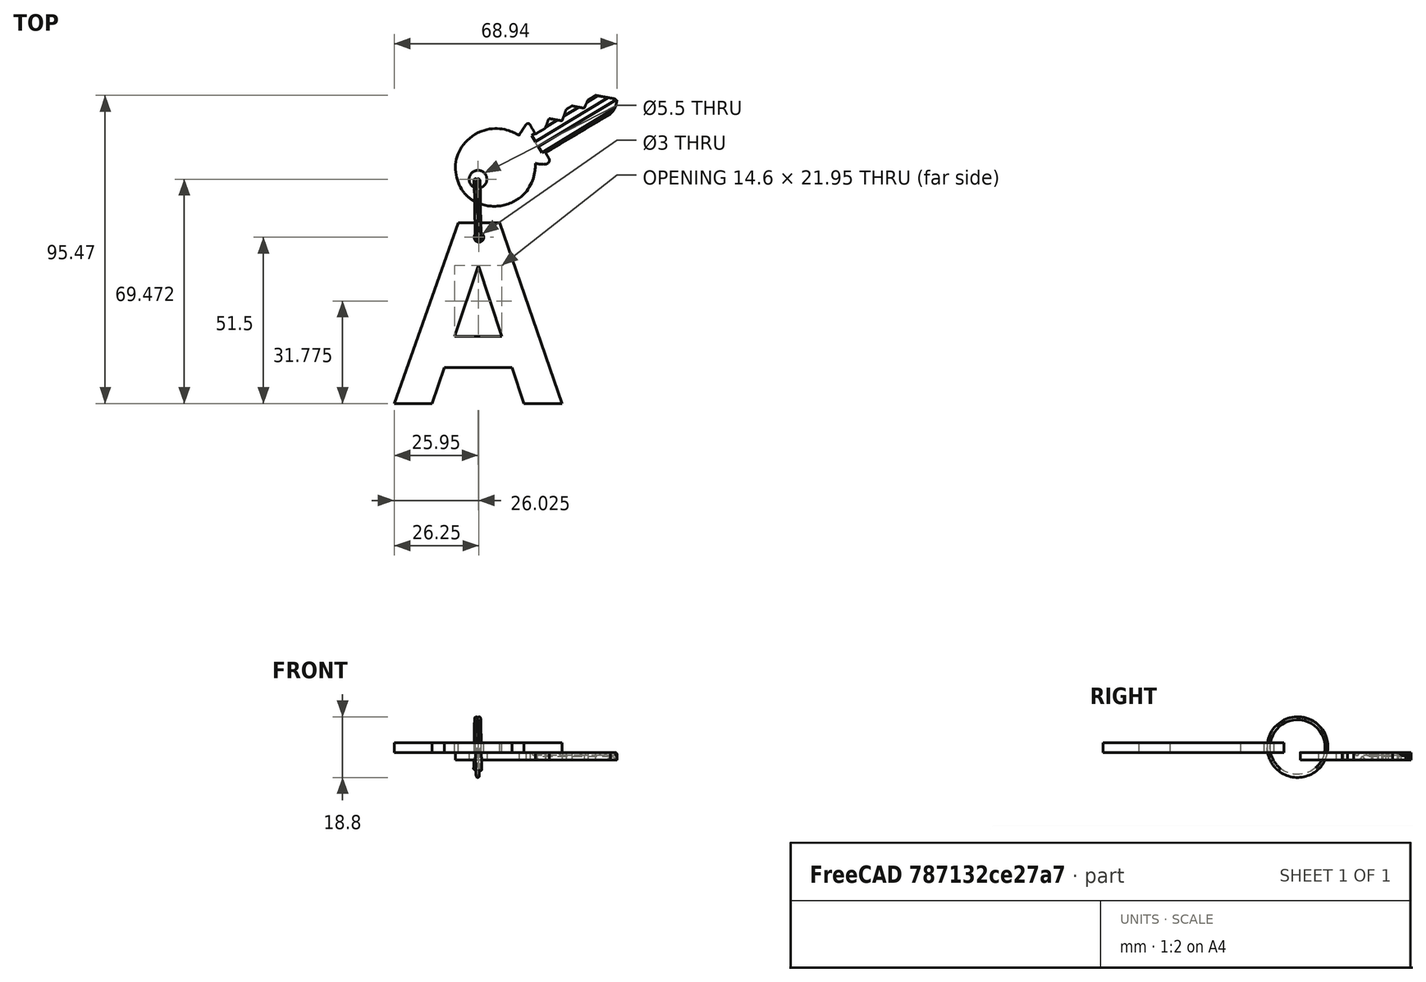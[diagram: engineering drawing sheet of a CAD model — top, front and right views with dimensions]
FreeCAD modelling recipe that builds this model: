
FCSTD DOCUMENT  (FreeCAD 0.15R4556 (Git))
Label: letter-A
License: CreativeCommons Attribution-ShareAlike
LicenseURL: http://creativecommons.org/licenses/by-sa/4.0/
objects: App::DocumentObjectGroup×2, Part::Feature×2, Part::Part2DObjectPython×1, Part::Extrusion×1, Part::Cylinder×1, Part::Cut×1, Part::FeaturePython×1
note: 7 computed .brp shape members not serialized (recipe doc carries the construction recipe); baked Part::Feature solids carry a one-line shape summary decoded from their .brp

FEATURE [Part::Part2DObjectPython] ShapeString  label="letter-A-string"  # Draft 2D object (typed FeaturePython)
  FontFile = <path>
  Placement = pos=(-2,1,0) rot=(0,0,1;0rad)
  Size = 30
  String = A
  Tracking = 0
FEATURE [Part::Extrusion] Extrude  label="letter-A-main"
  Base = -> ShapeString
  Dir = (0,0,3)
  Solid = true
FEATURE [Part::Cylinder] Cylinder001  label="cylinder-drill"
  Angle = 360
  Height = 10
  Placement = pos=(25.025,52.5,-5) rot=(0,0,1;0rad)
  Radius = 1.5
FEATURE [Part::Cut] Cut  label="letter-A-key-chain"
  Base = -> Extrude
  Placement = pos=(-25.025,-52.5,0) rot=(0,0,1;0rad)
  Tool = -> Cylinder001
FEATURE [App::DocumentObjectGroup] Group  label="letter-A-key-chain-src"
  Group = -> [Cut]
FEATURE [Part::FeaturePython] Clone  label="Clone of letter-A-key-chain"  # Draft clone (typed FeaturePython)
  Objects = -> [Cut]
  Placement = pos=(-25.025,-52.5,0) rot=(0,0,1;0rad)
  Scale = (1,1,1)
FEATURE [Part::Feature] Sweep  label="key-ring-model-1"
  Placement = pos=(-1.2,8.75462,1.6391) rot=(0.333333,0.881918,0.333333;1.69612rad)
  shape: bbox 3.31 x 27.02 x 26.33 mm, 4 faces (baked)
FEATURE [Part::Feature] Cut001  label="key-model-1"
  Placement = pos=(-5.39235,14.8947,0) rot=(0.963291,0.268461,0;3.14159rad)
  shape: bbox 51.09 x 35.14 x 2.3 mm, 44 faces (baked)
FEATURE [App::DocumentObjectGroup] Group001  label="Assembly"
  Group = -> [Clone,Sweep,Cut001]
note: 1 file-system path scrubbed to <path> (originals preserved in the JSON sidecar)
